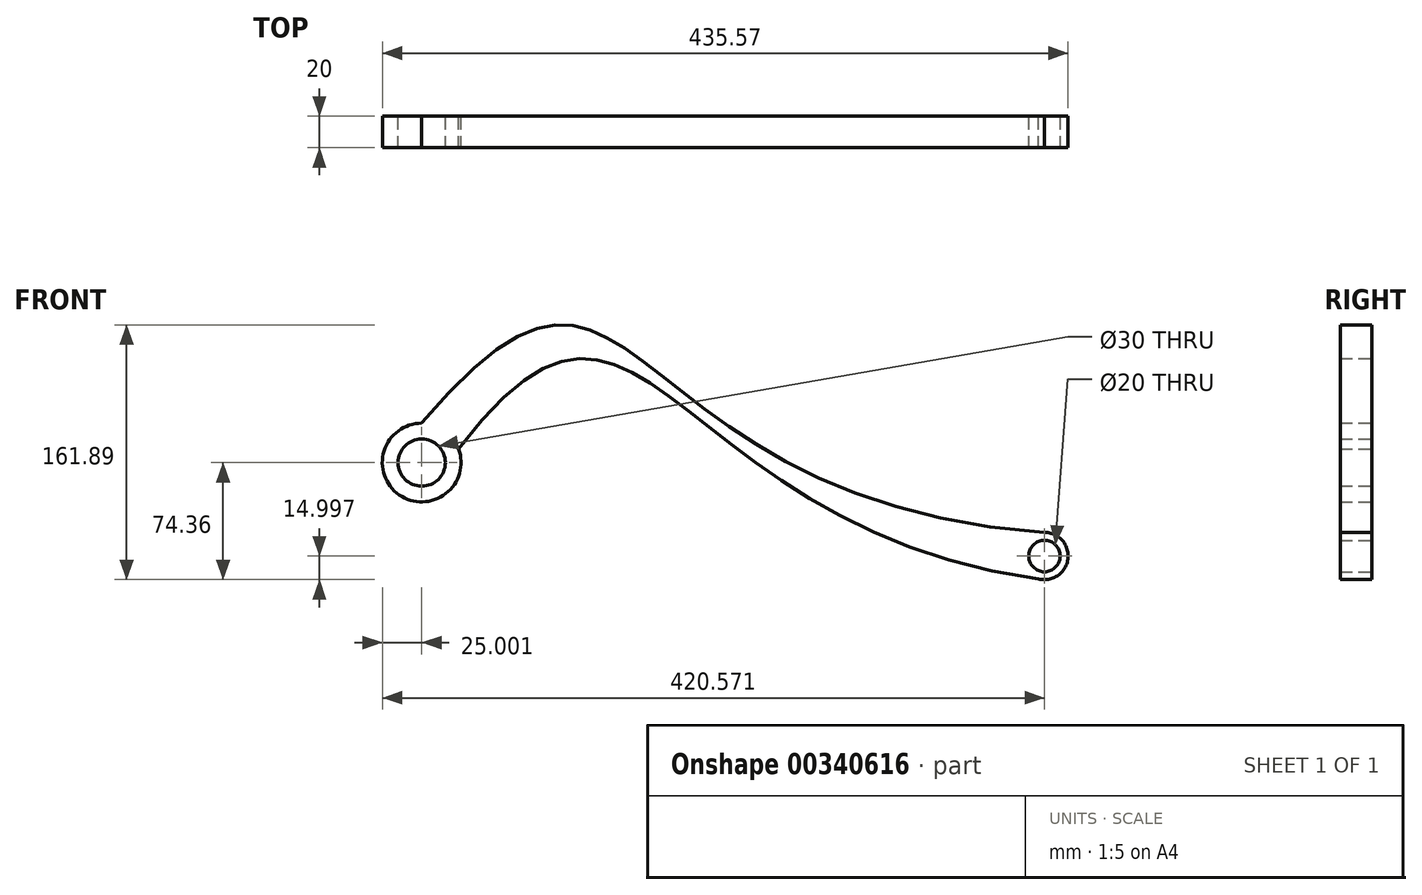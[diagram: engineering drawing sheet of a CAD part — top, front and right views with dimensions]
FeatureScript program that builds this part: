
annotation { "Feature Type Name" : "Feature", "Feature Type Description" : "" }
export const myFeature = defineFeature(function(context is Context, id is Id, definition is map)
    precondition{}
    {
        {
            var Q0;
            Q0=qCreatedBy(makeId("Front.planeOp"),FACE);
            var sketch = newSketch(context, id + "F0", { "sketchPlane" : qUnion([Q0])});
            skCircle(sketch, "E0", {"center": v(-140.59, 0) * mm, "radius": 15 * mm});
            skCircle(sketch, "E1", {"center": v(-140.59, 0) * mm, "radius": 25 * mm});
            skCircle(sketch, "E2", {"center": v(254.98, -59.36) * mm, "radius": 10 * mm});
            skCircle(sketch, "E3", {"center": v(254.98, -59.36) * mm, "radius": 15 * mm});
            skLineSegment(sketch, "E4", {"start": v(-140.59, 0) * mm, "end": v(254.98, -59.36) * mm, "construction": true});
            skPoint(sketch, "E5", {"position": v(-140.59, 25) * mm});
            skPoint(sketch, "E6", {"position": v(-140.59, -25) * mm});
            skPoint(sketch, "E7", {"position": v(254.98, -74.36) * mm});
            skPoint(sketch, "E8", {"position": v(254.98, -44.36) * mm});
            skFitSpline(sketch, "E9", {"points": [v(-140.59, 25) * mm, v(254.98, -44.36) * mm], "startDerivative": vector(421.77, 499.49) * mm, "endDerivative": vector(834.5, -58.09) * mm});
            skFitSpline(sketch, "E10", {"points": [v(-140.59, -25) * mm, v(254.98, -74.36) * mm], "startDerivative": vector(421.77, 649.49) * mm, "endDerivative": vector(764.94, -97.3) * mm});
            skSolve(sketch);
        }
        {
            var Q0;
            Q0 = qSketchRegion(id + "F0", true);
            extrude(context, id + "F1", {"entities" : qUnion([Q0]), "depth" : 20 * mm});
        }
    });
